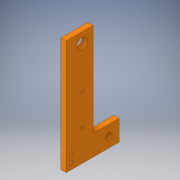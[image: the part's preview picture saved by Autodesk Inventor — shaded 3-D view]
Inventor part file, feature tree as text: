
AUTODESK INVENTOR PART (.ipt)
format: ipt  version: 2019 (Build 230136000, 136)  size: 147,456 bytes
history: native  units: in
note: dims shown in document units (in); Inventor stores cm internally (conversion verified against a paired STEP export)
features: sketch x4, extrude x2, hole x2, projected_geometry x2
ambient origin geometry x8: Origin, YZ Plane, XZ Plane, XY Plane, X Axis, Y Axis, Z Axis, Center Point
bodies: Solid1 (feature_tree)
feature tree (10):
  extrude  "Extrusion1"  Depth=5.5in
  hole  "Hole1"  [1 undecoded]
  extrude  "Extrusion2"  Depth=0.5in
  hole  "Hole2"  [1 undecoded]
  sketch  "Sketch1"  dims[d0=5.5in d2=0.5in]
  sketch  "Sketch2"  dims[d3=0.32in d5=4.5in]
  sketch  "Sketch3"  dims[d6=0.5in d7=0.5in]
  projected_geometry  "Projected Loop1"
  sketch  "Sketch4"  dims[d8=0.522in d9=0.5in d10=0.25in d11=0.0in d12=3.0in d13=1.5in d14=1.044in d15=0.522in d16=0.522in d17=0.15in d18=0.75in d19=0.375in d20=0.25in d21=0.5635in d22=1.0in d23=0.8108in d24=1.044in d26=1.272in d27=0.25in d28=0.0in d29=0.375in d30=0.3125in d31=2.3125in d32=2.3125in d33=0.15in d34=0.75in d35=0.375in d36=0.25in d37=0.5635in d38=1.0in d39=0.8108in]
  projected_geometry  "Projected Loop2"
note: 2 required parameter values undecoded (feature->parameter linkage not recoverable at this tier; creation-order binding heuristic only, values carry confidence <= 0.55)
